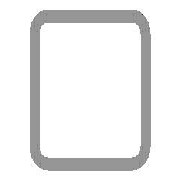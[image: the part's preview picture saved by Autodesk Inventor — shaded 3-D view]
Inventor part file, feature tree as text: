
AUTODESK INVENTOR PART (.ipt)
format: ipt  version: 2025 (Build 290162010, 162A)  size: 133,120 bytes
history: native  units: mm (DEFAULTED — no unit token found)
features: other x4, sketch x1, plane x1
ambient origin geometry x8: Origin, YZ Plane, XZ Plane, XY Plane, X Axis, Y Axis, Z Axis, Center Point
bodies: Solid1 (feature_tree), Body (feature_tree)
feature tree (6):
  parser-record x1  (decoder bookkeeping rows leaked as tree rows — omitted from the tree; the rows remain in map.json)
  other  "Driven Length"
  other  "Start Plane"
  other  "End Plane"
  sketch  "Sketch3"  dims[d3=540.0mm d4=0.0mm d7=6.0mm d9=50.0mm d11=50.0mm d12=3.0mm d13=20.0mm d14=560.0mm d15=25.0mm d16=25.0mm d17=90.0deg d18=540.0mm]
  plane  "Work Plane3"
